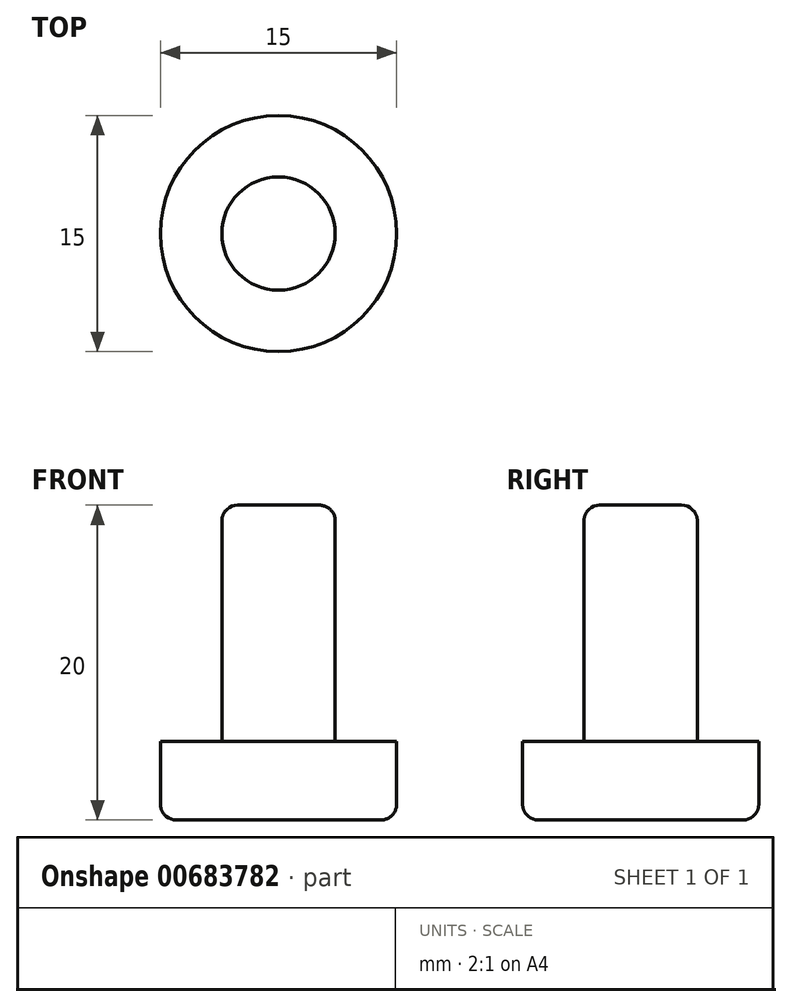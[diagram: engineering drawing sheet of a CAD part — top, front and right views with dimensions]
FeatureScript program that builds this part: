
annotation { "Feature Type Name" : "Feature", "Feature Type Description" : "" }
export const myFeature = defineFeature(function(context is Context, id is Id, definition is map)
    precondition{}
    {
        {
            var Q0;
            Q0=qCreatedBy(makeId("Top.planeOp"),FACE);
            var sketch = newSketch(context, id + "F0", { "sketchPlane" : qUnion([Q0])});
            skCircle(sketch, "E0", {"center": v(0, 0) * mm, "radius": 7.5 * mm});
            skCircle(sketch, "E1", {"center": v(0, 0) * mm, "radius": 3.6 * mm});
            skSolve(sketch);
        }
        {
            var Q0;
            Q0=makeQuery(id+"F0.imprint","IMPRINT",FACE,{"disambiguationData":[TD([[makeQuery(id+"F0.imprint","IMPRINT",EDGE,{"derivedFrom":sQuery(id+"F0.wireOp",EDGE,"E1")}),1.0]])]});
            extrude(context, id + "F1", {"entities" : qUnion([Q0]), "depth" : 15 * mm, "offsetDistance" : 25 * mm});
        }
        {
            var Q0;
            Q0 = qSketchRegion(id + "F0", true);
            var Q1;
            Q1=makeQuery(id+"F0.imprint","IMPRINT",FACE,{"disambiguationData":[TD([[makeQuery(id+"F0.imprint","IMPRINT",EDGE,{"derivedFrom":sQuery(id+"F0.wireOp",EDGE,"E1")}),1.0]])]});
            extrude(context, id + "F2", {"entities" : qUnion([Q0, Q1]), "operationType" : NewBodyOperationType.ADD, "oppositeDirection" : true, "depth" : 5 * mm, "offsetDistance" : 25 * mm});
        }
        {
            var Q0;
            Q0=makeQuery(id+"F1.opExtrude","CAP_EDGE",EDGE,{"disambiguationData":[OSD([sQuery(id+"F0.wireOp",EDGE,"E1")])],"isStart":false});
            var Q1;
            Q1=makeQuery(id+"F2.opExtrude","CAP_EDGE",EDGE,{"disambiguationData":[OSD([sQuery(id+"F0.wireOp",EDGE,"E0")])],"isStart":false});
            fillet(context, id + "F3", {"entities" : qUnion([Q0, Q1]), "radius" : 1 * mm, "tangentPropagation" : true, "allowEdgeOverflow" : false});
        }
    });
